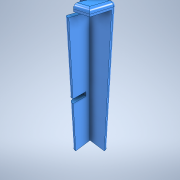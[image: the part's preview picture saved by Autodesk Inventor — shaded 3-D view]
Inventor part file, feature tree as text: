
AUTODESK INVENTOR PART (.ipt)
format: ipt  version: 2021 (Build 250183000, 183)  size: 167,936 bytes
history: native  units: mm
features: extrude x5, sketch x5, fillet x1
ambient origin geometry x8: Origin, YZ Plane, XZ Plane, XY Plane, X Axis, Y Axis, Z Axis, Center Point
bodies: Solid1 (feature_tree)
feature tree (11):
  extrude  "Extrusion1"  Depth=15.0mm
  extrude  "Extrusion3"  Depth=3.0mm
  extrude  "Extrusion4"  Depth=12.0mm
  fillet  "Fillet3"  Radius=3.0mm
  extrude  "Extrusion7"  Depth=12.0mm TaperAngle=0.0deg
  extrude  "Extrusion8"  Depth=6.1mm TaperAngle=0.0deg
  sketch  "Sketch1"  dims[d0=15.0mm d1=15.0mm]
  sketch  "Sketch4"  dims[d2=86.0mm d3=0.0mm d10=3.0mm]
  sketch  "Sketch6"  dims[d11=12.0mm d12=12.0mm d13=3.0mm]
  sketch  "Sketch11"  dims[d14=3.1mm d15=0.0mm d16=12.0mm d17=0.0mm]
  sketch  "Sketch12"  dims[d18=2.0mm d31=6.1mm d32=0.0mm d46=0.0mm d47=0.0mm d49=3.1mm d50=9.0mm]
